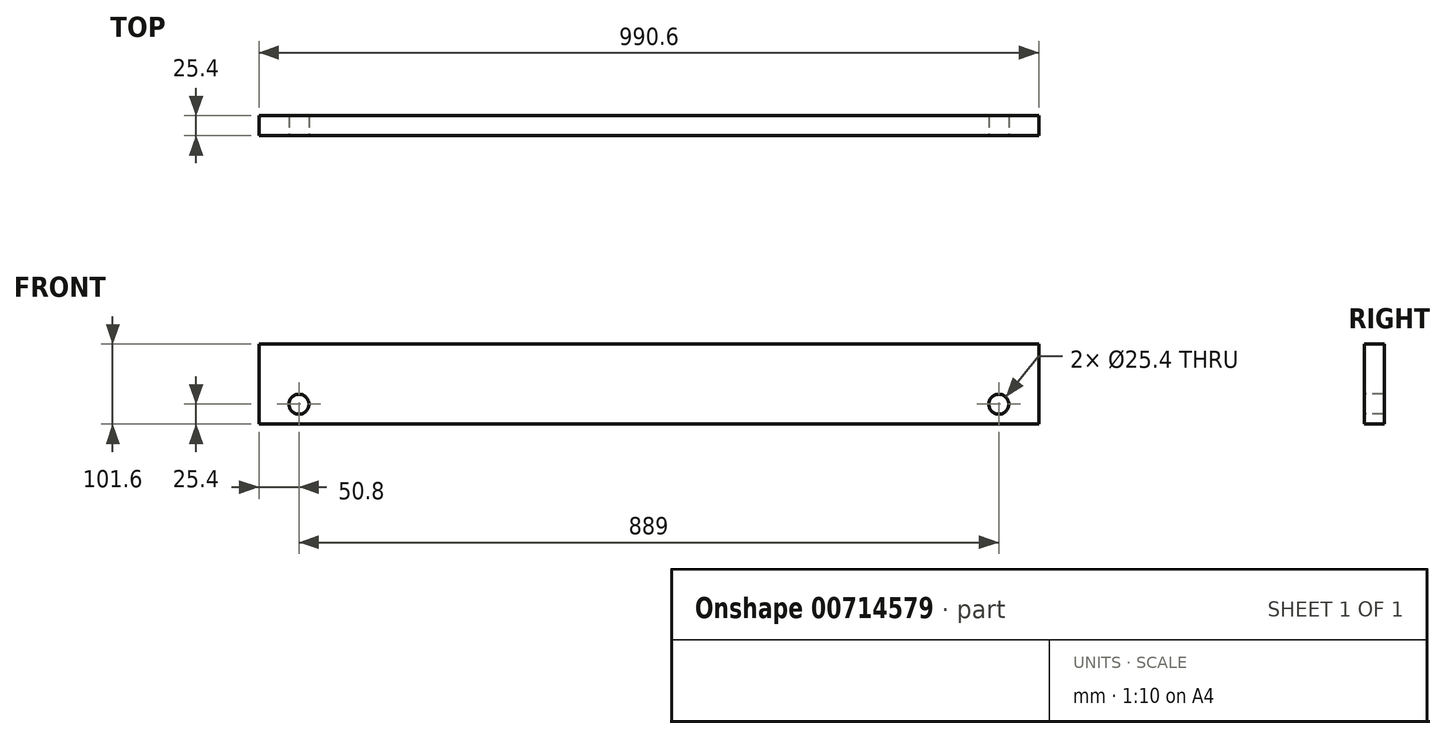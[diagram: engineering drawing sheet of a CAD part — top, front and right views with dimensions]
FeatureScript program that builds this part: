
annotation { "Feature Type Name" : "Feature", "Feature Type Description" : "" }
export const myFeature = defineFeature(function(context is Context, id is Id, definition is map)
    precondition{}
    {
        {
            var Q0;
            Q0=qCreatedBy(makeId("Front.planeOp"),FACE);
            var sketch = newSketch(context, id + "F0", { "sketchPlane" : qUnion([Q0])});
            skLineSegment(sketch, "E0.bottom", {"start": v(0, 101.6) * mm, "end": v(990.6, 101.6) * mm});
            skLineSegment(sketch, "E0.top", {"start": v(0, 0) * mm, "end": v(990.6, 0) * mm});
            skLineSegment(sketch, "E0.left", {"start": v(0, 101.6) * mm, "end": v(0, 0) * mm});
            skLineSegment(sketch, "E0.right", {"start": v(990.6, 101.6) * mm, "end": v(990.6, 0) * mm});
            skSolve(sketch);
        }
        {
            var Q0;
            Q0=makeQuery(id+"F0.imprint","IMPRINT",FACE,{"disambiguationData":[TD([[makeQuery(id+"F0.imprint","IMPRINT",EDGE,{"derivedFrom":sQuery(id+"F0.wireOp",EDGE,"E0.bottom")}),-1.0]])]});
            extrude(context, id + "F1", {"entities" : qUnion([Q0]), "depth" : 25.4 * mm, "offsetDistance" : 25.4 * mm});
        }
        {
            var Q0;
            Q0=makeQuery(id+"F1.opExtrude","CAP_FACE",FACE,{"disambiguationData":[OSD([sQuery(id+"F0.wireOp",EDGE,"E0.bottom"),sQuery(id+"F0.wireOp",EDGE,"E0.top"),sQuery(id+"F0.wireOp",EDGE,"E0.left"),sQuery(id+"F0.wireOp",EDGE,"E0.right")])],"isStart":false});
            var sketch = newSketch(context, id + "F2", { "sketchPlane" : qUnion([Q0])});
            skLineSegment(sketch, "E1", {"start": v(0, 50.8) * mm, "end": v(50.8, 50.8) * mm, "construction": true});
            skLineSegment(sketch, "E2", {"start": v(990.6, 50.8) * mm, "end": v(939.8, 50.8) * mm, "construction": true});
            skLineSegment(sketch, "E3", {"start": v(50.8, 101.6) * mm, "end": v(50.8, 50.8) * mm});
            skLineSegment(sketch, "E4", {"start": v(50.8, 50.8) * mm, "end": v(50.8, 0) * mm});
            skPoint(sketch, "E5", {"position": v(50.8, 25.4) * mm});
            skPoint(sketch, "E6", {"position": v(50.8, 76.2) * mm});
            skCircle(sketch, "E7", {"center": v(50.8, 25.4) * mm, "radius": 12.7 * mm});
            skLineSegment(sketch, "E8", {"start": v(939.8, 101.6) * mm, "end": v(939.8, 50.8) * mm});
            skLineSegment(sketch, "E9", {"start": v(939.8, 50.8) * mm, "end": v(939.8, 0) * mm});
            skPoint(sketch, "E10", {"position": v(939.8, 25.4) * mm});
            skPoint(sketch, "E11", {"position": v(939.8, 76.2) * mm});
            skCircle(sketch, "E12", {"center": v(939.8, 25.4) * mm, "radius": 12.7 * mm});
            skSolve(sketch);
        }
        {
            var Q0;
            Q0 = qSketchRegion(id + "F2", true);
            extrude(context, id + "F3", {"entities" : qUnion([Q0]), "operationType" : NewBodyOperationType.REMOVE, "endBound" : BoundingType.THROUGH_ALL, "oppositeDirection" : true, "depth" : 25.4 * mm, "offsetDistance" : 25.4 * mm});
        }
    });
